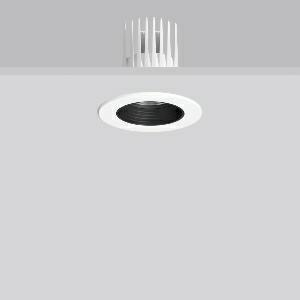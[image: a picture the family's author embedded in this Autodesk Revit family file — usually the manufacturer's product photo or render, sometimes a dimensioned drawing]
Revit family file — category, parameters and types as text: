
# Revit family: heledon_mini_e_901753_002_1_76_c6cc
name_source: partatom
category: Lighting Fixtures
units: mm (PartAtom-declared; Revit-internal decimal feet)

## family parameters
Cut with Voids When Loaded = No
Host = Face
Light Source = No
Part Type = Normal
Room Calculation Point = No
Round Connector Dimension = Use Diameter
Shared = No

## types (1)
- HELEDON mini E (1 x LED Modul 940, 3000 lm, 4000)
    Apparent Load = 29 VA
    Approval mark = CE
    CIE Flux Codes = 98 100 100 100 100
    Color Rendering = 92
    Color Temperature = 4000
    Default Elevation = 1800 mm
    Description = Series: HELEDON mini
Round recessed downlight. Housing: die-cast aluminium, powder-coated. Black plastic ring and recessed LED to prevent glare from the side. Optical assembly with lens made of plastic (polycarbonate) for the best homogeneous light distribution - can be changed without tools. Best colour rendering index Ra>90. Suitable for Recessed ceiling mounting. Installation without tools thanks to spring fastening system. Including separate LED converter with connecting cable 600 mm.High quality converter without flickering and stroboscopic effect. Through-wiring box (5 pole) available as accessory. The following accessories can be mounted without use of tools: interchangeable lenses, decorative glasses, honeycomb louvre, clear and frosted diffusers, white interchangeable plastic ring. 
Colour: traffic white, matt (RAL 9016)
Diameter: 124 mm
Height: 3 mm
Cut-out diameter: 114 mm
Recess height: 170 mm
Luminaire: recess height: 120 mm
Lamp: LED
Socket: without socket
Colour temperature: 4000K
Colour rendering index (CRI): 92
System power: 29 W
Rated luminous flux: 3000 lm
Luminous efficiency: 103 lm/W
Control gear: Converter, dimmable, DALI
Protection class: II
Type of protection: IP 20
    Height = 0 mm  [stored 0 ft]
    Lamp = 1 x LED Modul 940
    Lamp Light Flux = 3000 lm
    Lamp count = 1
    Length = 124 mm  [stored 0.406824 ft]
    Lifetime = 50000 h
    Luminous efficacy = 103 lm/W
    Manufacturer = RZB
    ModVariant = No
    Model = 901753.002.1.76
    Mounting Place = Ceiling
    Mounting Type = Recessed
    Number of Poles = 1
    OnlyDefault = Yes
    Power Factor = 1
    Product Name = HELEDON mini E
    Product group = Recessed downlights
    ProductGroupID = 402
    Protection Class = Protection class II
    Protection Degree = IP 20
    RLX_Detail_Level = 1
    RLX_Emergency_Light_Flux = 0 lm
    RLX_Emergency_Type = 0
    RLX_Emergency_Type_DB = No
    RlxData = <blob elided: 124661 chars, md5=daf967d5>
    Socket = socket
    Standby Power = 0 W
    System Light Flux = 3000 lm
    System Power = 29 W
    Type Comments = Product without accessories
    Type Image = 901656.002.jpg
    URL = http://relux.com
    VarID = ---
    Voltage = 230 V
    Voltage Range = 220-240 V
    Weight = 0.00 kg
    Width = 0 mm  [stored 0 ft]

note: [stored X ft] marks values corroborated as IEEE doubles in the binary element streams (Revit-internal decimal feet)

## geometry (parser evidence)
native form markers: Blend x4, Sweep x11
no freeform markers — native parametric forms only
